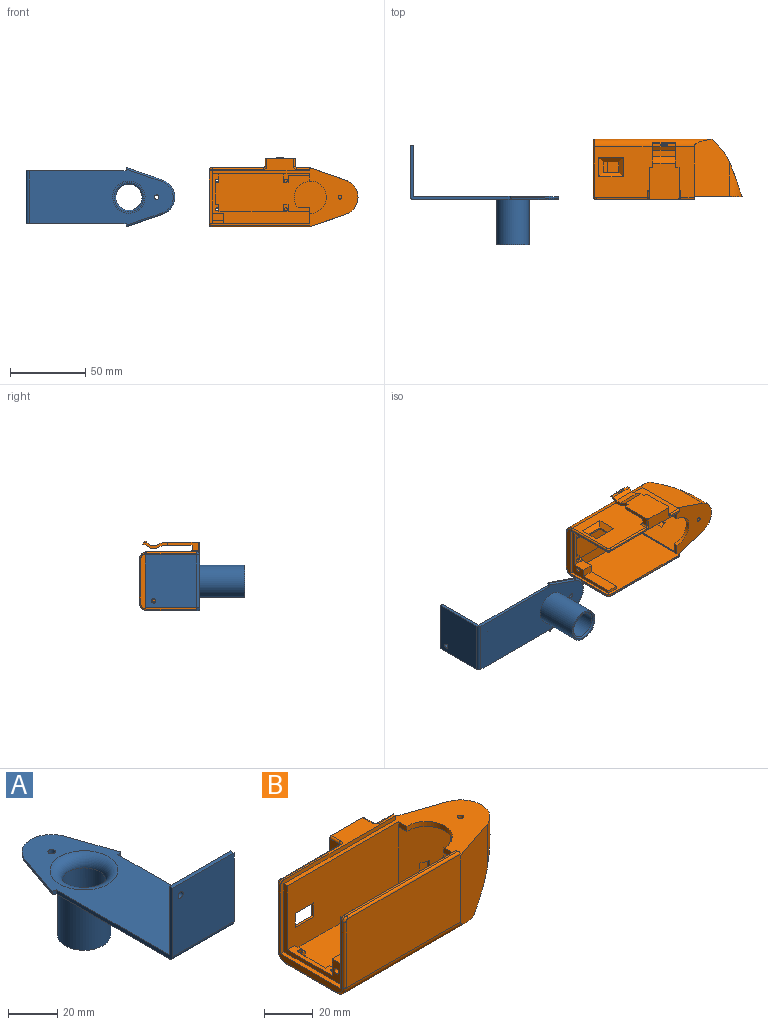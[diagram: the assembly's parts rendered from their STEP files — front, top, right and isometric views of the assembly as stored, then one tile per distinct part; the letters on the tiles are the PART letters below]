
ASSEMBLY  parts=2 mates=3
PART A: 28 faces, bbox 39x99.8x66 mm
  f0: plane 96.78x39mm, normal (0,0,1), area 2516.3mm2, adj f1,f2,f3,f4,f5,f6,f7,f9
  f1: plane 66.39x36mm, normal (1,0,0), area 199.9mm2, adj f0,f2,f8,f10,f16,f17,f18
  f2: plane 2x2mm, normal (0.32,-0.95,0), area 4mm2, adj f0,f1,f3,f10,f19
  f3: plane 23.63x8.16mm, normal (0.95,0.33,0), area 25mm2, adj f0,f2,f4,f19
  f4: cylinder r=12mm len=22.69mm, axis (0,0,-1), area 29.7mm2, adj f0,f3,f5,f20
  f5: plane 23.63x8.16mm, normal (-0.95,0.33,0), area 25mm2, adj f0,f4,f6,f21
  f6: plane 2x2mm, normal (-0.32,-0.95,0), area 4mm2, adj f0,f5,f7,f10,f21
  f7: plane 66.39x36mm, normal (-1,0,0), area 199.9mm2, adj f0,f6,f8,f10,f16,f17,f18
  f8: plane 35x34mm, normal (0,-1,0), area 1182.9mm2, adj f1,f7,f17,f18,f22
  f9: cylinder r=1.5mm len=3mm, axis (0,0,-1), area 18.8mm2, adj f0,f10
  f10: plane 95.78x37.1mm, normal (0,0,-1), area 2692.7mm2, adj f1,f2,f6,f7,f9,f11,f18,f19
  f11: cylinder r=10.75mm len=30mm, axis (0,0,1), area 2026.3mm2, adj f10,f12
  f12: plane 21.5x21.5mm, normal (0,0,-1), area 64.4mm2, adj f11,f15
  f13: cylinder r=8.75mm len=26mm, axis (0,0,-1), area 1429.4mm2, adj f14,f15
  f14: torus R=13.75mm, axis (0,0,1), area 521.5mm2, adj f0,f13
  f15: torus R=9.75mm, axis (0,0,-1), area 89.9mm2, adj f12,f13
  f16: plane 35x34mm, normal (0,1,0), area 1182.9mm2, adj f0,f1,f7,f17,f22
  f17: plane 35x2mm, normal (0,0,1), area 70mm2, adj f1,f7,f8,f16
  f18: cylinder r=2mm len=35mm, axis (1,0,0), area 110mm2, adj f1,f7,f8,f10
  f19: cylinder r=1mm len=23.96mm, axis (-0.33,0.95,0), area 39.3mm2, adj f2,f3,f10,f20
  f20: torus R=11mm, axis (0,0,1), area 45.3mm2, adj f4,f10,f19,f21
  f21: cylinder r=1mm len=23.96mm, axis (-0.33,-0.95,0), area 39.3mm2, adj f5,f6,f10,f20
  f22: cylinder r=1.5mm len=3mm, axis (0,-1,0), area 18.8mm2, adj f8,f16
  f23: plane 4x1.5mm, normal (0,1,0), area 6mm2, adj f0,f24,f26,f27
  f24: plane 6x1.5mm, normal (-1,0,0), area 9mm2, adj f0,f23,f25,f27
  f25: plane 4x1.5mm, normal (0,-1,0), area 6mm2, adj f0,f24,f26,f27
  f26: plane 6x1.5mm, normal (1,0,0), area 9mm2, adj f0,f23,f25,f27
  f27: plane 6x4mm, normal (0,0,1), area 24mm2, adj f23,f24,f25,f26
PART B: 156 faces, bbox 100.1x47.5x41.8 mm
  f0: plane 3.12x2mm, normal (0,1,0), area 6.2mm2, adj f1,f2,f52,f55
  f1: plane 11.5x6mm, normal (1,0,0), area 55.6mm2, adj f0,f2,f5,f56,f106,f132,f134,f135
  f2: plane 26x7.5mm, normal (0,0,1), area 75.2mm2, adj f0,f1,f36,f40,f41,f48,f49,f50
  f3: plane 37x37mm, normal (-1,0,0), area 172.1mm2, adj f4,f35,f87,f88,f98,f99,f100,f101
  f4: plane 66.33x37mm, normal (0,1,0), area 2188.8mm2, adj f3,f14,f29,f30,f33,f56,f88,f106
  f5: plane 56.83x3mm, normal (0,-1,0), area 63mm2, adj f1,f7,f26,f53,f55,f56,f130
  f6: plane 32x6.51mm, normal (1,0,0), area 52.6mm2, adj f8,f10,f36,f55,f113,f117,f118,f119
  f7: plane 9x1.5mm, normal (1,0,0), area 6.8mm2, adj f5,f9,f55,f56,f111,f114
  f8: cylinder r=10.5mm len=17.49mm, axis (0,0,-1), area 11.8mm2, adj f6,f9,f55,f119
  f9: plane 11.5x1.5mm, normal (0,1,0), area 15.2mm2, adj f7,f8,f55,f107,f111,f119
  f10: plane 17.09x5.89mm, normal (0,0,1), area 31.3mm2, adj f6,f36,f42,f46,f47,f128,f129
  f11: plane 34.18x24.41mm, normal (-0.33,-0.95,0), area 698.6mm2, adj f13,f111,f113,f116,f117,f118,f124,f125
  f12: plane 34.18x24.41mm, normal (-0.33,0.95,0), area 698.6mm2, adj f13,f111,f112,f114,f115,f117,f120,f121
  f13: extruded ~33x26.28mm, area 598.9mm2, adj f11,f12,f110,f111,f115,f116,f117
  f14: plane 35x6.76mm, normal (-1,0,0), area 33.8mm2, adj f4,f15,f16,f56,f112,f114,f117
  f15: cylinder r=10.75mm len=21.5mm, axis (0,0,1), area 86.8mm2, adj f14,f16,f27,f117
  f16: plane 96.72x39mm, normal (0,0,1), area 819.6mm2, adj f14,f15,f17,f18,f19,f20,f27,f33
  f17: plane 37.92x23.63mm, normal (0.33,-0.95,0), area 851.8mm2, adj f16,f20,f21,f31,f91
  f18: plane 37.92x23.63mm, normal (0.33,0.95,0), area 851.8mm2, adj f16,f19,f22,f25,f91
  f19: cylinder r=12mm len=22.43mm, axis (0,0,-1), area 166.7mm2, adj f16,f18,f91
  f20: cylinder r=12mm len=22.43mm, axis (0,0,-1), area 166.7mm2, adj f16,f17,f91
  f21: cylinder r=5mm len=77.81mm, axis (1,0,0), area 558.4mm2, adj f17,f31,f32,f91,f100
  f22: cylinder r=5mm len=77.81mm, axis (-1,0,0), area 558.4mm2, adj f18,f25,f32,f91,f101
  f23: plane 2.5x2mm, normal (0,0,-1), area 5mm2, adj f58,f59,f60,f63
  f24: plane 20x3.5mm, normal (0,0,-1), area 70mm2, adj f57,f58,f60,f79
  f25: plane 66x34mm, normal (0,1,0), area 1919.3mm2, adj f18,f22,f34,f78,f79,f80,f85,f86
  f26: plane 4.86x3.08mm, normal (0,0,1), area 11.8mm2, adj f5,f44,f53,f54,f130
  f27: plane 4.76x2.5mm, normal (-1,0,0), area 11.9mm2, adj f15,f16,f36,f117
  f28: plane 64.66x8.5mm, normal (0,0,1), area 201.2mm2, adj f34,f35,f59,f87,f92,f93,f95,f103
  f29: plane 7.5x2mm, normal (0,0,1), area 15mm2, adj f4,f37,f106,f131
  f30: plane 64.66x1mm, normal (0,0,1), area 64.5mm2, adj f4,f33,f88,f94
  f31: plane 66x34mm, normal (0,-1,0), area 2243.8mm2, adj f17,f21,f33,f94,f96,f98
  f32: plane 77.72x29mm, normal (0,0,-1), area 2247.5mm2, adj f21,f22,f40,f41,f91,f102
  f33: plane 2.14x2.14mm, normal (0.95,0.32,0), area 4mm2, adj f4,f16,f30,f31,f94
  f34: plane 2.14x2.14mm, normal (0.95,-0.32,0), area 4mm2, adj f16,f25,f28,f35,f103
  f35: plane 66.33x36mm, normal (0,-1,0), area 199.8mm2, adj f3,f16,f28,f34,f87,f131,f133
  f36: plane 64.33x34mm, normal (0,-1,0), area 2070.7mm2, adj f2,f6,f10,f16,f27,f47,f48,f55
  f37: plane 23.5x7.5mm, normal (0,1,0), area 176.3mm2, adj f29,f106,f131,f132
  f38: cylinder r=1.25mm len=6.5mm, axis (0,0,1), area 51.1mm2, adj f16,f39
  f39: plane 2.5x2.5mm, normal (0,0,1), area 4.9mm2, adj f38
  f40: cylinder r=1mm len=6mm, axis (0,0,1), area 37.7mm2, adj f2,f32
  f41: cylinder r=1mm len=6mm, axis (0,0,1), area 37.7mm2, adj f2,f32
  f42: cylinder r=1mm len=2mm, axis (0,0,-1), area 12.6mm2, adj f10,f43
  f43: plane 2x2mm, normal (0,0,1), area 3.1mm2, adj f42
  f44: cylinder r=1mm len=2mm, axis (0,0,-1), area 12.6mm2, adj f26,f45
  f45: plane 2x2mm, normal (0,0,1), area 3.1mm2, adj f44
  f46: plane 3.08x2mm, normal (0,-1,0), area 6.2mm2, adj f10,f47,f55,f128
  f47: plane 5.89x2mm, normal (-1,0,0), area 11.8mm2, adj f10,f36,f46,f55
  f48: plane 5.89x2mm, normal (1,0,0), area 11.8mm2, adj f2,f36,f49,f55
  f49: plane 2.5x2mm, normal (0,-1,0), area 5mm2, adj f2,f48,f50,f55
  f50: plane 14.25x2mm, normal (1,0,0), area 28.5mm2, adj f2,f49,f51,f55
  f51: plane 2.5x2mm, normal (0,1,0), area 5mm2, adj f2,f50,f52,f55
  f52: plane 4.86x2mm, normal (1,0,0), area 9.7mm2, adj f0,f2,f51,f55
  f53: plane 4.86x2mm, normal (-1,0,0), area 9.7mm2, adj f5,f26,f54,f55
  f54: plane 3.08x2mm, normal (0,1,0), area 6.2mm2, adj f26,f53,f55,f130
  f55: plane 62.45x25mm, normal (0,0,1), area 1339mm2, adj f0,f5,f6,f7,f8,f9,f36,f46
  f56: plane 56.83x8mm, normal (0,0,1), area 454.6mm2, adj f1,f4,f5,f7,f14,f106
  f57: plane 20x5.5mm, normal (1,0,0), area 54mm2, adj f24,f59,f60,f61,f80,f105
  f58: plane 20x5.5mm, normal (-1,0,0), area 54mm2, adj f23,f24,f59,f60,f78,f92
  f59: plane 24x20mm, normal (0,1,0), area 464.6mm2, adj f23,f28,f57,f58,f61,f62,f63,f65
  f60: plane 20x19mm, normal (0,-1,0), area 365mm2, adj f23,f24,f57,f58,f61,f62,f63,f66
  f61: plane 2.5x2mm, normal (0,0,-1), area 5mm2, adj f57,f59,f60,f62
  f62: plane 16.69x4.22mm, normal (1,0,0), area 31.1mm2, adj f59,f60,f61,f64,f65,f66,f67,f68
  f63: plane 16.69x4.22mm, normal (-1,0,0), area 31.1mm2, adj f23,f59,f60,f64,f65,f66,f67,f68
  f64: plane 15x4mm, normal (0,1,0), area 60mm2, adj f62,f63,f65,f72
  f65: plane 15x4.53mm, normal (0,0.9,-0.44), area 75.7mm2, adj f59,f62,f63,f64
  f66: plane 15x4.53mm, normal (0,-0.9,0.44), area 75.7mm2, adj f60,f62,f63,f67
  f67: plane 15x4mm, normal (0,-1,0), area 60mm2, adj f62,f63,f66,f68
  f68: plane 15x3.6mm, normal (0,-0.82,-0.57), area 66mm2, adj f62,f63,f67,f69
  f69: plane 15x1.55mm, normal (0,-1,0), area 23.3mm2, adj f62,f63,f68,f70
  f70: plane 15x1.15mm, normal (0,0.5,-0.86), area 19.9mm2, adj f62,f63,f69,f71
  f71: plane 15x2mm, normal (0,1,0), area 25mm2, adj f62,f63,f70,f72,f73,f74,f75,f76
  f72: plane 15x2.49mm, normal (0,0.83,0.56), area 45mm2, adj f62,f63,f64,f71
  f73: plane 5x1mm, normal (0,0,1), area 5mm2, adj f71,f74,f76,f77
  f74: plane 1x1mm, normal (1,0,0), area 1mm2, adj f71,f73,f75,f77
  f75: plane 5x1mm, normal (0,0,-1), area 5mm2, adj f71,f74,f76,f77
  f76: plane 1x1mm, normal (-1,0,0), area 1mm2, adj f71,f73,f75,f77
  f77: plane 5x1mm, normal (0,1,0), area 5mm2, adj f73,f74,f75,f76
  f78: cylinder r=1mm len=5mm, axis (0,0,1), area 7.1mm2, adj f25,f58,f79,f93
  f79: cylinder r=1mm len=22mm, axis (-1,0,0), area 33mm2, adj f24,f25,f78,f80
  f80: cylinder r=1mm len=5mm, axis (0,0,-1), area 7.1mm2, adj f25,f57,f79,f104
  f81: plane 10.5x1mm, normal (0,0,1), area 10.5mm2, adj f36,f82,f83,f90
  f82: plane 7x1mm, normal (-1,0,0), area 7mm2, adj f36,f81,f84,f86
  f83: plane 7x1mm, normal (1,0,0), area 7mm2, adj f36,f81,f84,f85
  f84: plane 10.5x1mm, normal (0,0,-1), area 10.5mm2, adj f36,f82,f83,f89
  f85: plane 13x3mm, normal (0.71,0.71,0), area 42.4mm2, adj f25,f83,f89,f90
  f86: plane 13x3mm, normal (-0.71,0.71,0), area 42.4mm2, adj f25,f82,f89,f90
  f87: cylinder r=2mm len=2mm, axis (0,1,0), area 3.1mm2, adj f3,f28,f35,f97
  f88: cylinder r=2mm len=2mm, axis (0,1,0), area 3.1mm2, adj f3,f4,f30,f96
  f89: plane 16.5x3mm, normal (0,0.71,-0.71), area 57.3mm2, adj f25,f84,f85,f86
  f90: plane 16.5x3mm, normal (0,0.71,0.71), area 57.3mm2, adj f25,f81,f85,f86
  f91: extruded ~38x30.84mm, area 915.3mm2, adj f17,f18,f19,f20,f21,f22,f32
  f92: cylinder r=1mm len=5.5mm, axis (0,-1,0), area 8.6mm2, adj f28,f58,f59,f93
  f93: torus R=2mm, axis (0,0,1), area 3.4mm2, adj f28,f78,f92,f95
  f94: cylinder r=1mm len=65mm, axis (-1,0,0), area 101.8mm2, adj f30,f31,f33,f96
  f95: cylinder r=1mm len=34mm, axis (1,0,0), area 53.4mm2, adj f25,f28,f93,f97
  f96: torus R=1mm, axis (0,1,0), area 4mm2, adj f31,f88,f94,f98
  f97: torus R=1mm, axis (0,1,0), area 4mm2, adj f25,f87,f95,f99
  f98: cylinder r=1mm len=33mm, axis (0,0,1), area 51.8mm2, adj f3,f31,f96,f100
  f99: cylinder r=1mm len=33mm, axis (0,0,-1), area 51.8mm2, adj f3,f25,f97,f101
  f100: torus R=4mm, axis (-1,0,0), area 11.4mm2, adj f3,f21,f98,f102
  f101: torus R=4mm, axis (-1,0,0), area 11.4mm2, adj f3,f22,f99,f102
  f102: cylinder r=1mm len=29mm, axis (0,-1,0), area 45.6mm2, adj f3,f32,f100,f101
  f103: cylinder r=1mm len=9mm, axis (1,0,0), area 13.9mm2, adj f25,f28,f34,f104
  f104: torus R=2mm, axis (0,0,1), area 3.4mm2, adj f28,f80,f103,f105
  f105: cylinder r=1mm len=5.5mm, axis (0,1,0), area 8.6mm2, adj f28,f57,f59,f104
  f106: plane 35x2mm, normal (1,0,0), area 70mm2, adj f1,f4,f29,f37,f56
  f107: plane 19.11x1mm, normal (1,0,0), area 19.1mm2, adj f9,f109,f111,f119
  f108: plane 4.39x1mm, normal (1,0,0), area 3.8mm2, adj f109,f111,f118,f119
  f109: plane 3.09x1mm, normal (0,1,0), area 3.1mm2, adj f107,f108,f111,f119
  f110: cylinder r=3.75mm len=27.76mm, axis (0,0,1), area 505mm2, adj f13,f117
  f111: plane 29x26.03mm, normal (0,0,1), area 581mm2, adj f7,f9,f11,f12,f13,f107,f108,f109
  f112: plane 30.5x0.25mm, normal (0,1,0), area 7.7mm2, adj f12,f14,f114,f117
  f113: plane 30.5x0.25mm, normal (0,-1,0), area 7.7mm2, adj f6,f11,f117,f118
  f114: cylinder r=2.5mm len=7.49mm, axis (1,0,0), area 11.3mm2, adj f7,f12,f14,f111,f112
  f115: cylinder r=9.5mm len=15.28mm, axis (0,0,-1), area 54.8mm2, adj f12,f13,f117
  f116: cylinder r=9.5mm len=15.28mm, axis (0,0,-1), area 54.8mm2, adj f11,f13,f117
  f117: plane 34x28.8mm, normal (0,0,-1), area 453.6mm2, adj f6,f11,f12,f13,f14,f15,f27,f110
  f118: cylinder r=2.5mm len=22.08mm, axis (-1,0,0), area 45.1mm2, adj f6,f11,f108,f111,f113,f119
  f119: plane 23.5x14.59mm, normal (0,0,-1), area 138mm2, adj f6,f8,f9,f107,f108,f109,f118
  f120: plane 4.23x1.46mm, normal (0,0,1), area 3.1mm2, adj f12,f122,f123
  f121: plane 4.23x1.46mm, normal (0,0,-1), area 3.1mm2, adj f12,f122,f123
  f122: plane 4x1.46mm, normal (-1,0,0), area 5.8mm2, adj f12,f120,f121,f123
  f123: plane 4.23x4mm, normal (0,1,0), area 16.9mm2, adj f12,f120,f121,f122
  f124: plane 4.23x4mm, normal (0,-1,0), area 16.9mm2, adj f11,f125,f126,f127
  f125: plane 4x1.46mm, normal (-1,0,0), area 5.8mm2, adj f11,f124,f126,f127
  f126: plane 4.23x1.46mm, normal (0,0,-1), area 3.1mm2, adj f11,f124,f125
  f127: plane 4.23x1.46mm, normal (0,0,1), area 3.1mm2, adj f11,f124,f125
  f128: plane 4.72x2mm, normal (1,0,0), area 9.4mm2, adj f10,f46,f55,f129
  f129: plane 14.01x2mm, normal (0,-1,0), area 28mm2, adj f6,f10,f55,f128
  f130: plane 4.86x2mm, normal (1,0,0), area 9.7mm2, adj f5,f26,f54,f55
  f131: plane 35x34mm, normal (-1,0,0), area 235.6mm2, adj f2,f4,f16,f29,f35,f36,f37,f132
  f132: plane 7.5x5mm, normal (0,0,1), area 37.5mm2, adj f1,f37,f131,f135
  f133: plane 35x2mm, normal (0,0,1), area 70mm2, adj f3,f4,f35,f131
  f134: cylinder r=1.25mm len=7.5mm, axis (-1,0,0), area 58.9mm2, adj f1,f131
  f135: plane 8.5x7.5mm, normal (0,1,0), area 63.8mm2, adj f1,f2,f131,f132
  f136: plane 15.07x0.5mm, normal (0,0,-1), area 7.5mm2, adj f137,f138,f139,f140
  f137: plane 15.07x0.04mm, normal (0,1,0), area 0.5mm2, adj f136,f138,f139,f140
  f138: cylinder r=3.5mm len=0.5mm, axis (0,0,1), area 0mm2, adj f136,f137,f139
  f139: cylinder r=3.5mm len=15.07mm, axis (-1,0,0), area 7.5mm2, adj f136,f137,f138,f140
  f140: cylinder r=3.5mm len=0.5mm, axis (0,0,-1), area 0mm2, adj f136,f137,f139
  f141: plane 1x0.79mm, normal (-1,0,0), area 0.5mm2, adj f142,f147,f149
  f142: plane 3.5x1mm, normal (-1,0,0), area 3.4mm2, adj f141,f146,f147,f148,f149
  f143: plane 1x0.63mm, normal (-1,0,0), area 0.6mm2, adj f144,f146,f147,f148
  f144: cylinder r=3.5mm len=1.38mm, axis (0,0,1), area 1.6mm2, adj f143,f145,f147,f148
  f145: plane 6x1mm, normal (1,0,0), area 5.4mm2, adj f144,f147,f148,f149
  f146: plane 3.12x1mm, normal (0,-1,0), area 3.1mm2, adj f142,f143,f147,f148
  f147: plane 6x4.5mm, normal (0,0,-1), area 21.6mm2, adj f141,f142,f143,f144,f145,f146,f149
  f148: plane 4.5x4mm, normal (0,0,1), area 12.6mm2, adj f142,f143,f144,f145,f146,f149
  f149: cylinder r=2.5mm len=4.5mm, axis (1,0,0), area 10.4mm2, adj f141,f142,f145,f147,f148
  f150: plane 2.18x1mm, normal (-1,0,0), area 1.6mm2, adj f151,f152,f153,f155
  f151: plane 3.05x1.38mm, normal (0,0,-1), area 3.5mm2, adj f150,f152,f153,f154
  f152: cylinder r=2.5mm len=2mm, axis (-1,0,0), area 3.2mm2, adj f150,f151,f154,f155
  f153: cylinder r=3.5mm len=1.38mm, axis (0,0,1), area 1.6mm2, adj f150,f151,f154,f155
  f154: plane 3.05x1mm, normal (1,0,0), area 2.4mm2, adj f151,f152,f153,f155
  f155: plane 1.38x1.05mm, normal (0,0,1), area 0.7mm2, adj f150,f152,f153,f154
PLACE A rot(axis=(-0.58,-0.58,-0.58),120deg) t=(-136.34,-10.48,-45.16)mm
PLACE B rot(axis=(1,0,0),90deg) t=(-16.86,29.52,-45.16)mm fixed
MATE parallel A.f8 <-> B.f3  axis (-1,0,0) through (-171.03,8.45,-45.08)mm
MATE planar A.f0 <-> B.f16  axis (0,1,0) through (-128.67,-8.48,-45.27)mm
MATE planar A.f1 <-> B.f35  axis (0,0,1) through (-148.65,-3.35,-27.66)mm
